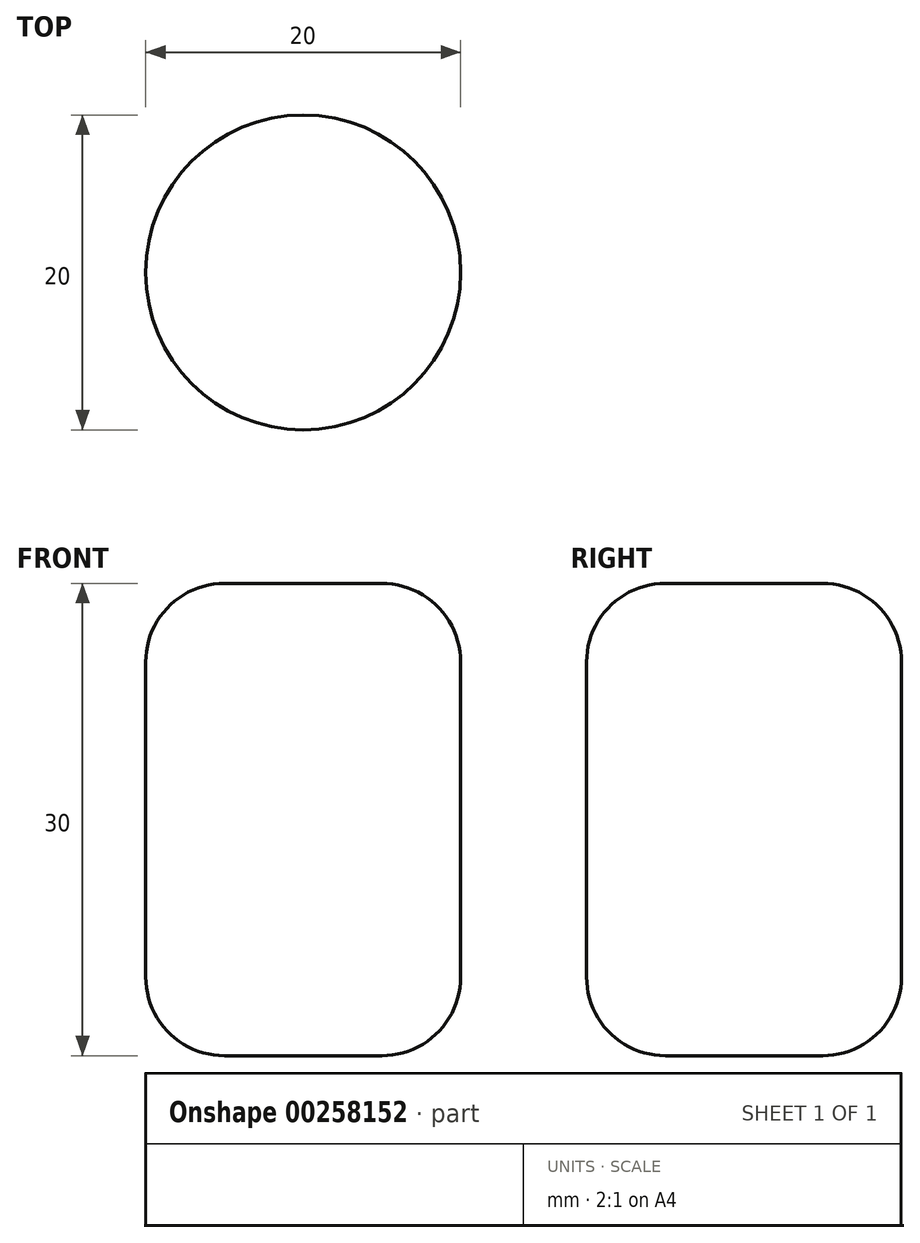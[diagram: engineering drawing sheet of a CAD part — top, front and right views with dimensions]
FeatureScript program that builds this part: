
annotation { "Feature Type Name" : "Feature", "Feature Type Description" : "" }
export const myFeature = defineFeature(function(context is Context, id is Id, definition is map)
    precondition{}
    {
        {
            var Q0;
            Q0=qCreatedBy(makeId("Top.planeOp"),FACE);
            var sketch = newSketch(context, id + "F0", { "sketchPlane" : qUnion([Q0])});
            skCircle(sketch, "E0", {"center": v(0, 0) * mm, "radius": 10 * mm});
            skSolve(sketch);
        }
        {
            var Q0;
            Q0=makeQuery(id+"F0.imprint","IMPRINT",FACE,{"disambiguationData":[TD([[makeQuery(id+"F0.imprint","IMPRINT",EDGE,{"derivedFrom":sQuery(id+"F0.wireOp",EDGE,"E0")}),1.0]])]});
            extrude(context, id + "F1", {"entities" : qUnion([Q0]), "depth" : 30 * mm});
        }
        {
            var Q0;
            Q0=makeQuery(id+"F1.opExtrude","CAP_EDGE",EDGE,{"disambiguationData":[OSD([sQuery(id+"F0.wireOp",EDGE,"E0")])],"isStart":false});
            var Q1;
            Q1=makeQuery(id+"F1.opExtrude","SWEPT_FACE",FACE,{"disambiguationData":[OSD([sQuery(id+"F0.wireOp",EDGE,"E0")])]});
            fillet(context, id + "F2", {"entities" : qUnion([Q0, Q1]), "radius" : 5 * mm, "tangentPropagation" : true, "allowEdgeOverflow" : false});
        }
    });
